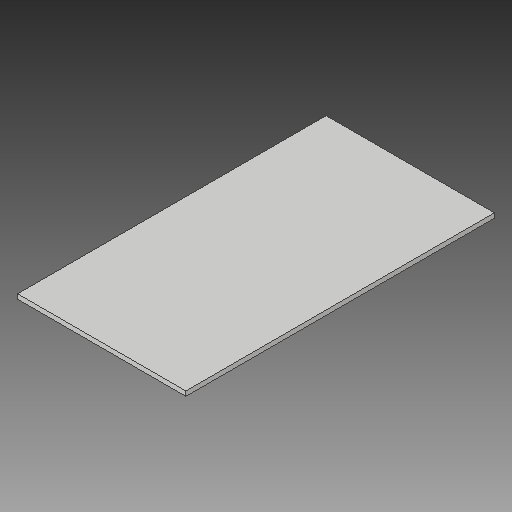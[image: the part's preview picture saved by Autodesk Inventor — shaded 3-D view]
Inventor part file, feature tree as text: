
AUTODESK INVENTOR PART (.ipt)
format: ipt  version: 2017 (Build 210142000, 142)  size: 90,624 bytes
history: native  units: in
note: dims shown in document units (in); Inventor stores cm internally (conversion verified against a paired STEP export)
features: extrude x1, sketch x1
ambient origin geometry x8: Origin, YZ Plane, XZ Plane, XY Plane, X Axis, Y Axis, Z Axis, Center Point
bodies: Solid1 (feature_tree)
feature tree (2):
  extrude  "Extrusion1"  Depth=66.0in
  sketch  "Sketch1"  dims[d0=36.0in d1=66.0in d2=1.0in d3=0.0in]
